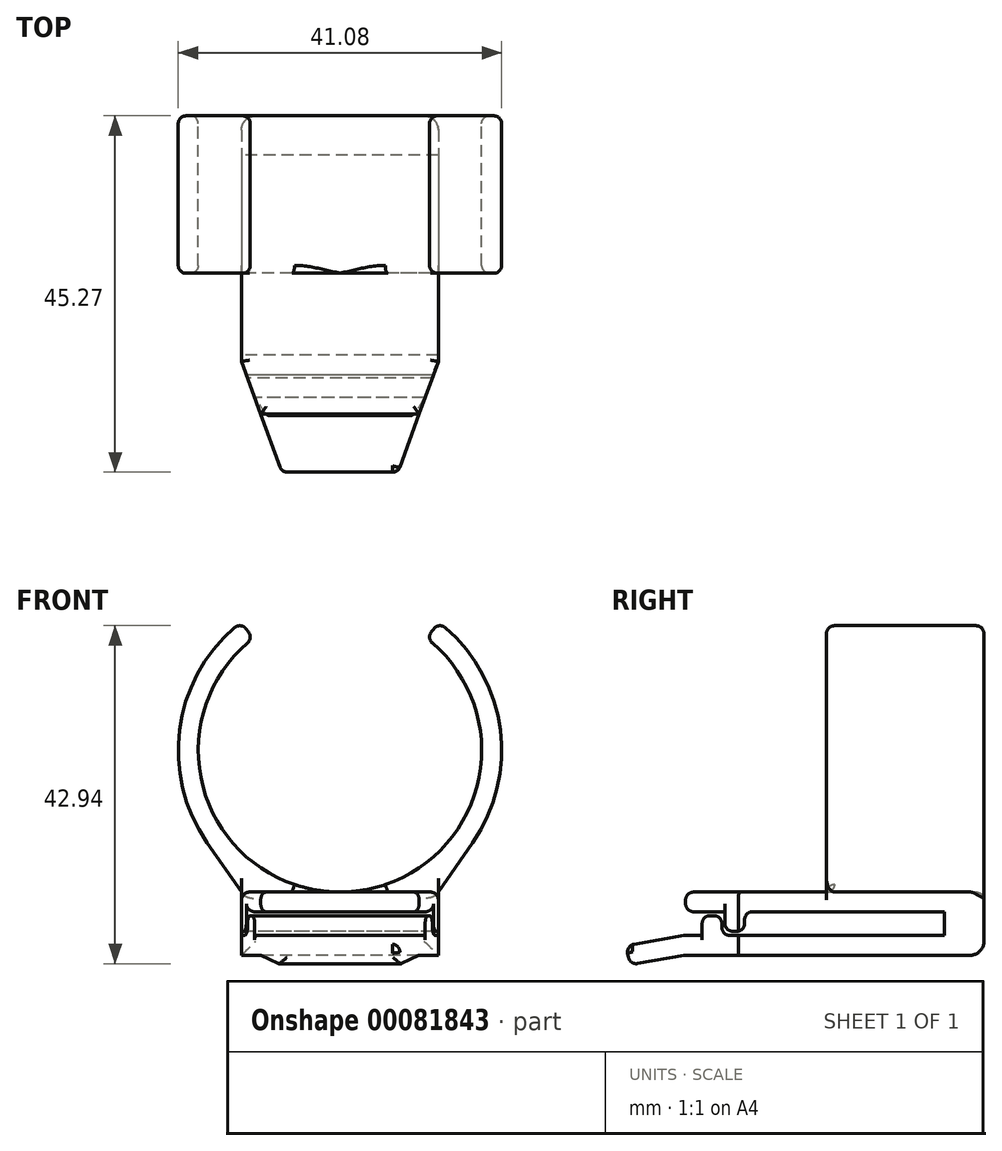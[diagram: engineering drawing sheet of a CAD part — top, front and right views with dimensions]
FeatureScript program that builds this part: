
annotation { "Feature Type Name" : "Feature", "Feature Type Description" : "" }
export const myFeature = defineFeature(function(context is Context, id is Id, definition is map)
    precondition{}
    {
        {
            var Q0;
            Q0=qCreatedBy(makeId("Right.planeOp"),FACE);
            var sketch = newSketch(context, id + "F0", { "sketchPlane" : qUnion([Q0])});
            skLineSegment(sketch, "E0.bottom", {"start": v(0, 0) * mm, "end": v(-38.1, 0) * mm});
            skLineSegment(sketch, "E0.top", {"start": v(-5, 2.54) * mm, "end": v(-33.3, 2.54) * mm});
            skLineSegment(sketch, "E0.left", {"start": v(0, 0) * mm, "end": v(0, 2.54) * mm});
            skLineSegment(sketch, "E1", {"start": v(-38.1, 0) * mm, "end": v(-45, -1.22) * mm});
            skLineSegment(sketch, "E2", {"start": v(-45, -1.22) * mm, "end": v(-45.43, 1.25) * mm});
            skLineSegment(sketch, "E3", {"start": v(-38.1, 2.54) * mm, "end": v(-45.43, 1.25) * mm});
            skLineSegment(sketch, "E4", {"start": v(-35.43, 0) * mm, "end": v(-38.1, 0) * mm, "construction": true});
            skLineSegment(sketch, "E5", {"start": v(-38.1, 0) * mm, "end": v(-38.1, 2.54) * mm, "construction": true});
            skLineSegment(sketch, "E6.top", {"start": v(0, 8.04) * mm, "end": v(0, 8.04) * mm});
            skLineSegment(sketch, "E6.left", {"start": v(0, 2.54) * mm, "end": v(0, 8.04) * mm});
            skLineSegment(sketch, "E6.right", {"start": v(-5, 2.54) * mm, "end": v(-5, 5.54) * mm});
            skLineSegment(sketch, "E7.bottom", {"start": v(0, 8.04) * mm, "end": v(-37.9, 8.04) * mm});
            skLineSegment(sketch, "E7.top", {"start": v(-5, 5.54) * mm, "end": v(-30.4, 5.54) * mm});
            skLineSegment(sketch, "E7.right", {"start": v(-37.9, 8.04) * mm, "end": v(-37.9, 5.54) * mm});
            skLineSegment(sketch, "E8.top", {"start": v(-32.9, 3.04) * mm, "end": v(-30.4, 3.04) * mm});
            skLineSegment(sketch, "E8.left", {"start": v(-32.9, 5.54) * mm, "end": v(-32.9, 3.04) * mm});
            skLineSegment(sketch, "E8.right", {"start": v(-30.4, 5.54) * mm, "end": v(-30.4, 3.04) * mm});
            skLineSegment(sketch, "E9.trimOffspring", {"start": v(-32.9, 5.54) * mm, "end": v(-37.9, 5.54) * mm});
            skLineSegment(sketch, "E10", {"start": v(-33.3, 2.54) * mm, "end": v(-33.3, 5.04) * mm});
            skLineSegment(sketch, "E11", {"start": v(-33.3, 5.04) * mm, "end": v(-35.8, 5.04) * mm});
            skLineSegment(sketch, "E12", {"start": v(-35.8, 5.04) * mm, "end": v(-35.8, 2.54) * mm});
            skLineSegment(sketch, "E13.trimOffspring", {"start": v(-35.8, 2.54) * mm, "end": v(-38.1, 2.54) * mm});
            skSolve(sketch);
        }
        {
            var Q0;
            Q0 = qSketchRegion(id + "F0", true);
            extrude(context, id + "F1", {"entities" : qUnion([Q0]), "depth" : 25 * mm});
        }
        {
            var Q0;
            Q0=makeQuery(id+"F1.opExtrude","SWEPT_FACE",FACE,{"disambiguationData":[OSD([sQuery(id+"F0.wireOp",EDGE,"E0.left"),sQuery(id+"F0.wireOp",EDGE,"E6.left")])]});
            var sketch = newSketch(context, id + "F2", { "sketchPlane" : qUnion([Q0])});
            skLineSegment(sketch, "E14", {"start": v(-12.5, 8.04) * mm, "end": v(-12.5, 44.73) * mm, "construction": true});
            skArc(sketch, "E15", {"start": v(-24.23, 39.69) * mm, "mid": v(-12.5, 8.04) * mm, "end": v(-0.77, 39.69) * mm});
            skLineSegment(sketch, "E16", {"start": v(-12.5, 8.04) * mm, "end": v(0, 8.04) * mm, "construction": true});
            skArc(sketch, "E17.0", {"start": v(4.36, 14.31) * mm, "mid": v(7.87, 28.65) * mm, "end": v(0.87, 41.63) * mm});
            skLineSegment(sketch, "E18", {"start": v(-25, 8.04) * mm, "end": v(0, 8.04) * mm});
            skLineSegment(sketch, "E19", {"start": v(0, 8.04) * mm, "end": v(4.36, 14.31) * mm});
            skLineSegment(sketch, "E20", {"start": v(-25, 8.04) * mm, "end": v(-29.36, 14.31) * mm});
            skLineSegment(sketch, "E21", {"start": v(-0.9, 41.06) * mm, "end": v(-0.57, 41.49) * mm});
            skPoint(sketch, "E22", {"position": v(-1.5, 40.29) * mm});
            skLineSegment(sketch, "E23.MirrorCS", {"start": v(-24.1, 41.06) * mm, "end": v(-24.43, 41.49) * mm});
            skArc(sketch, "E24.trimOffspring", {"start": v(-25.87, 41.63) * mm, "mid": v(-32.87, 28.65) * mm, "end": v(-29.36, 14.31) * mm});
            skPoint(sketch, "E25.visualSharp", {"position": v(-23.5, 40.29) * mm});
            skArc(sketch, "E25.filletArc", {"start": v(-24.23, 39.69) * mm, "mid": v(-23.9, 40.35) * mm, "end": v(-24.1, 41.06) * mm});
            skPoint(sketch, "E26.visualSharp", {"position": v(-25.05, 42.3) * mm});
            skArc(sketch, "E26.filletArc", {"start": v(-24.43, 41.49) * mm, "mid": v(-25.11, 41.87) * mm, "end": v(-25.87, 41.63) * mm});
            skArc(sketch, "E27.filletArc", {"start": v(-0.9, 41.06) * mm, "mid": v(-1.1, 40.35) * mm, "end": v(-0.77, 39.69) * mm});
            skPoint(sketch, "E28.visualSharp", {"position": v(0.05, 42.3) * mm});
            skArc(sketch, "E28.filletArc", {"start": v(0.87, 41.63) * mm, "mid": v(0.11, 41.87) * mm, "end": v(-0.57, 41.49) * mm});
            skSolve(sketch);
        }
        {
            var Q0;
            Q0 = qSketchRegion(id + "F2", true);
            extrude(context, id + "F3", {"entities" : qUnion([Q0]), "operationType" : NewBodyOperationType.ADD, "oppositeDirection" : true, "depth" : 20 * mm});
        }
        {
            var Q0;
            Q0=makeQuery(id+"F1.opExtrude","SWEPT_FACE",FACE,{"disambiguationData":[OSD([sQuery(id+"F0.wireOp",EDGE,"E0.bottom")])]});
            var sketch = newSketch(context, id + "F4", { "sketchPlane" : qUnion([Q0])});
            skLineSegment(sketch, "E29", {"start": v(12.5, 0) * mm, "end": v(12.5, 56.84) * mm, "construction": true});
            skLineSegment(sketch, "E30", {"start": v(12.5, 45.55) * mm, "end": v(19.78, 45.55) * mm});
            skLineSegment(sketch, "E31", {"start": v(19.78, 45.55) * mm, "end": v(26.83, 26.17) * mm});
            skLineSegment(sketch, "E32", {"start": v(26.83, 26.17) * mm, "end": v(31.87, 26.17) * mm});
            skLineSegment(sketch, "E33", {"start": v(31.87, 26.17) * mm, "end": v(31.87, 54.4) * mm});
            skLineSegment(sketch, "E34", {"start": v(31.87, 54.4) * mm, "end": v(12.5, 54.4) * mm});
            skLineSegment(sketch, "E35.MirrorCS", {"start": v(-6.87, 54.4) * mm, "end": v(12.5, 54.4) * mm});
            skLineSegment(sketch, "E36.MirrorCS", {"start": v(-6.87, 26.17) * mm, "end": v(-6.87, 54.4) * mm});
            skLineSegment(sketch, "E37.MirrorCS", {"start": v(-1.83, 26.17) * mm, "end": v(-6.87, 26.17) * mm});
            skLineSegment(sketch, "E38.MirrorCS", {"start": v(12.5, 45.55) * mm, "end": v(5.22, 45.55) * mm});
            skLineSegment(sketch, "E39.MirrorCS", {"start": v(5.22, 45.55) * mm, "end": v(-1.83, 26.17) * mm});
            skSolve(sketch);
        }
        {
            var Q0;
            Q0 = qSketchRegion(id + "F4", true);
            extrude(context, id + "F5", {"entities" : qUnion([Q0]), "operationType" : NewBodyOperationType.REMOVE, "oppositeDirection" : true, "depth" : 25 * mm, "hasSecondDirection" : true, "secondDirectionOppositeDirection" : false, "secondDirectionDepth" : 25 * mm});
        }
        {
            var Q0;
            Q0=makeQuery(id+"F1.opExtrude","SWEPT_EDGE",EDGE,{"disambiguationData":[OSD([sQuery(id+"F0.wireOp",EDGE,"E2"),sQuery(id+"F0.wireOp",EDGE,"E3")])]});
            var Q1;
            Q1=makeQuery(id+"F1.opExtrude","SWEPT_EDGE",EDGE,{"disambiguationData":[OSD([sQuery(id+"F0.wireOp",EDGE,"E1"),sQuery(id+"F0.wireOp",EDGE,"E2")])]});
            var Q2;
            Q2=makeQuery(id+"F5.boolean.opBoolean","INTERSECT",EDGE,{"derivedFrom":[makeQuery(id+"F1.opExtrude","SWEPT_FACE",FACE,{"disambiguationData":[OSD([sQuery(id+"F0.wireOp",EDGE,"E2")])]}),makeQuery(id+"F5.opExtrude","SWEPT_FACE",FACE,{"disambiguationData":[OSD([sQuery(id+"F4.wireOp",EDGE,"E39.MirrorCS")])]})]});
            var Q3;
            Q3=makeQuery(id+"F5.boolean.opBoolean","INTERSECT",EDGE,{"derivedFrom":[makeQuery(id+"F1.opExtrude","SWEPT_FACE",FACE,{"disambiguationData":[OSD([sQuery(id+"F0.wireOp",EDGE,"E2")])]}),makeQuery(id+"F5.opExtrude","SWEPT_FACE",FACE,{"disambiguationData":[OSD([sQuery(id+"F4.wireOp",EDGE,"E31")])]})]});
            var Q4;
            Q4=makeQuery(id+"F5.boolean.opBoolean","INTERSECT",EDGE,{"derivedFrom":[makeQuery(id+"F1.opExtrude","SWEPT_FACE",FACE,{"disambiguationData":[OSD([sQuery(id+"F0.wireOp",EDGE,"E3")])]}),makeQuery(id+"F5.opExtrude","SWEPT_FACE",FACE,{"disambiguationData":[OSD([sQuery(id+"F4.wireOp",EDGE,"E31")])]})]});
            var Q5;
            Q5=makeQuery(id+"F1.opExtrude","SWEPT_EDGE",EDGE,{"disambiguationData":[OSD([sQuery(id+"F0.wireOp",EDGE,"E7.bottom"),sQuery(id+"F0.wireOp",EDGE,"E7.right")])]});
            var Q6;
            Q6=makeQuery(id+"F5.boolean.opBoolean","INTERSECT",EDGE,{"derivedFrom":[makeQuery(id+"F1.opExtrude","SWEPT_FACE",FACE,{"disambiguationData":[OSD([sQuery(id+"F0.wireOp",EDGE,"E3")])]}),makeQuery(id+"F5.opExtrude","SWEPT_FACE",FACE,{"disambiguationData":[OSD([sQuery(id+"F4.wireOp",EDGE,"E39.MirrorCS")])]})]});
            var Q7;
            Q7=makeQuery(id+"F3.boolean.opBoolean","SPLIT",EDGE,{"derivedFrom":makeQuery(id+"F1.opExtrude","CAP_EDGE",EDGE,{"disambiguationData":[OSD([sQuery(id+"F0.wireOp",EDGE,"E7.bottom")])],"isStart":true})});
            var Q8;
            Q8=makeQuery(id+"F3.boolean.opBoolean","SPLIT",EDGE,{"derivedFrom":makeQuery(id+"F1.opExtrude","CAP_EDGE",EDGE,{"disambiguationData":[OSD([sQuery(id+"F0.wireOp",EDGE,"E7.bottom")])],"isStart":false})});
            var Q9;
            Q9=makeQuery(id+"F5.boolean.opBoolean","INTERSECT",EDGE,{"derivedFrom":[makeQuery(id+"F1.opExtrude","SWEPT_FACE",FACE,{"disambiguationData":[OSD([sQuery(id+"F0.wireOp",EDGE,"E7.bottom")])]}),makeQuery(id+"F5.opExtrude","SWEPT_FACE",FACE,{"disambiguationData":[OSD([sQuery(id+"F4.wireOp",EDGE,"E31")])]})]});
            var Q10;
            Q10=makeQuery(id+"F5.boolean.opBoolean","INTERSECT",EDGE,{"derivedFrom":[makeQuery(id+"F1.opExtrude","SWEPT_FACE",FACE,{"disambiguationData":[OSD([sQuery(id+"F0.wireOp",EDGE,"E7.bottom")])]}),makeQuery(id+"F5.opExtrude","SWEPT_FACE",FACE,{"disambiguationData":[OSD([sQuery(id+"F4.wireOp",EDGE,"E39.MirrorCS")])]})]});
            fillet(context, id + "F6", {"entities" : qUnion([Q0, Q1, Q2, Q3, Q4, Q5, Q6, Q7, Q8, Q9, Q10]), "radius" : 1 * mm, "tangentPropagation" : true, "allowEdgeOverflow" : false});
        }
        {
            var Q0;
            {var subQ0=sQuery(id+"F2.wireOp",EDGE,"E15");Q0=makeQuery(id+"F3.boolean.opBoolean","MERGE",EDGE,{"derivedFrom":[makeQuery(id+"F3.opExtrude","CAP_EDGE",EDGE,{"disambiguationData":[OSD([subQ0]),TDD([makeQuery(id+"F2.imprint","IMPRINT",EDGE,{"disambiguationData":[TD([[makeQuery(id+"F2.imprint","INTERSECT",VERTEX,{"derivedFrom":[subQ0,sQuery(id+"F2.wireOp",EDGE,"E25.filletArc")]}),-1.0]])],"derivedFrom":subQ0})])],"isStart":true}),makeQuery(id+"F3.opExtrude","CAP_EDGE",EDGE,{"disambiguationData":[OSD([subQ0]),TDD([makeQuery(id+"F2.imprint","IMPRINT",EDGE,{"disambiguationData":[TD([[makeQuery(id+"F2.imprint","INTERSECT",VERTEX,{"derivedFrom":[subQ0,sQuery(id+"F2.wireOp",EDGE,"E27.filletArc")]}),1.0]])],"derivedFrom":subQ0})])],"isStart":true})]});}
            var Q1;
            {var subQ0=sQuery(id+"F2.wireOp",EDGE,"E15");Q1=makeQuery(id+"F3.opExtrude","CAP_EDGE",EDGE,{"disambiguationData":[OSD([subQ0]),TDD([makeQuery(id+"F2.imprint","IMPRINT",EDGE,{"disambiguationData":[TD([[makeQuery(id+"F2.imprint","INTERSECT",VERTEX,{"derivedFrom":[subQ0,sQuery(id+"F2.wireOp",EDGE,"E25.filletArc")]}),-1.0]])],"derivedFrom":subQ0})])],"isStart":false});}
            fillet(context, id + "F7", {"entities" : qUnion([Q0, Q1]), "radius" : 1 * mm, "tangentPropagation" : true, "allowEdgeOverflow" : false});
        }
        {
            var Q0;
            Q0=makeQuery(id+"F1.opExtrude","CAP_EDGE",EDGE,{"disambiguationData":[OSD([sQuery(id+"F0.wireOp",EDGE,"E0.left"),sQuery(id+"F0.wireOp",EDGE,"E6.left")])],"isStart":false});
            var Q1;
            Q1=makeQuery(id+"F1.opExtrude","SWEPT_EDGE",EDGE,{"disambiguationData":[OSD([sQuery(id+"F0.wireOp",EDGE,"E0.bottom"),sQuery(id+"F0.wireOp",EDGE,"E0.left")])]});
            var Q2;
            Q2=makeQuery(id+"F1.opExtrude","CAP_EDGE",EDGE,{"disambiguationData":[OSD([sQuery(id+"F0.wireOp",EDGE,"E0.left"),sQuery(id+"F0.wireOp",EDGE,"E6.left")])],"isStart":true});
            fillet(context, id + "F8", {"entities" : qUnion([Q0, Q1, Q2]), "radius" : 1.8 * mm, "tangentPropagation" : true, "allowEdgeOverflow" : false});
        }
        {
            var Q0;
            Q0=makeQuery(id+"F1.opExtrude","SWEPT_EDGE",EDGE,{"disambiguationData":[OSD([sQuery(id+"F0.wireOp",EDGE,"E7.right"),sQuery(id+"F0.wireOp",EDGE,"E9.trimOffspring")])]});
            var Q1;
            Q1=makeQuery(id+"F5.boolean.opBoolean","INTERSECT",EDGE,{"derivedFrom":[makeQuery(id+"F1.opExtrude","SWEPT_FACE",FACE,{"disambiguationData":[OSD([sQuery(id+"F0.wireOp",EDGE,"E9.trimOffspring")])]}),makeQuery(id+"F5.opExtrude","SWEPT_FACE",FACE,{"disambiguationData":[OSD([sQuery(id+"F4.wireOp",EDGE,"E31")])]})]});
            var Q2;
            Q2=makeQuery(id+"F5.boolean.opBoolean","INTERSECT",EDGE,{"derivedFrom":[makeQuery(id+"F1.opExtrude","SWEPT_FACE",FACE,{"disambiguationData":[OSD([sQuery(id+"F0.wireOp",EDGE,"E9.trimOffspring")])]}),makeQuery(id+"F5.opExtrude","SWEPT_FACE",FACE,{"disambiguationData":[OSD([sQuery(id+"F4.wireOp",EDGE,"E39.MirrorCS")])]})]});
            fillet(context, id + "F9", {"entities" : qUnion([Q0, Q1, Q2]), "radius" : 1 * mm, "tangentPropagation" : true, "allowEdgeOverflow" : false});
        }
        {
            var Q0;
            Q0=makeQuery(id+"F1.opExtrude","SWEPT_EDGE",EDGE,{"disambiguationData":[OSD([sQuery(id+"F0.wireOp",EDGE,"E10"),sQuery(id+"F0.wireOp",EDGE,"E11")])]});
            var Q1;
            Q1=makeQuery(id+"F1.opExtrude","SWEPT_EDGE",EDGE,{"disambiguationData":[OSD([sQuery(id+"F0.wireOp",EDGE,"E8.top"),sQuery(id+"F0.wireOp",EDGE,"E8.right")])]});
            var Q2;
            Q2=makeQuery(id+"F1.opExtrude","SWEPT_EDGE",EDGE,{"disambiguationData":[OSD([sQuery(id+"F0.wireOp",EDGE,"E8.top"),sQuery(id+"F0.wireOp",EDGE,"E8.left")])]});
            var Q3;
            Q3=makeQuery(id+"F1.opExtrude","SWEPT_EDGE",EDGE,{"disambiguationData":[OSD([sQuery(id+"F0.wireOp",EDGE,"E11"),sQuery(id+"F0.wireOp",EDGE,"E12")])]});
            var Q4;
            Q4=makeQuery(id+"F1.opExtrude","SWEPT_EDGE",EDGE,{"disambiguationData":[OSD([sQuery(id+"F0.wireOp",EDGE,"E0.top"),sQuery(id+"F0.wireOp",EDGE,"E10")])]});
            var Q5;
            Q5=makeQuery(id+"F1.opExtrude","SWEPT_EDGE",EDGE,{"disambiguationData":[OSD([sQuery(id+"F0.wireOp",EDGE,"E7.top"),sQuery(id+"F0.wireOp",EDGE,"E8.right")])]});
            fillet(context, id + "F10", {"entities" : qUnion([Q0, Q1, Q2, Q3, Q4, Q5]), "radius" : 1 * mm, "tangentPropagation" : true, "allowEdgeOverflow" : false});
        }
    });
